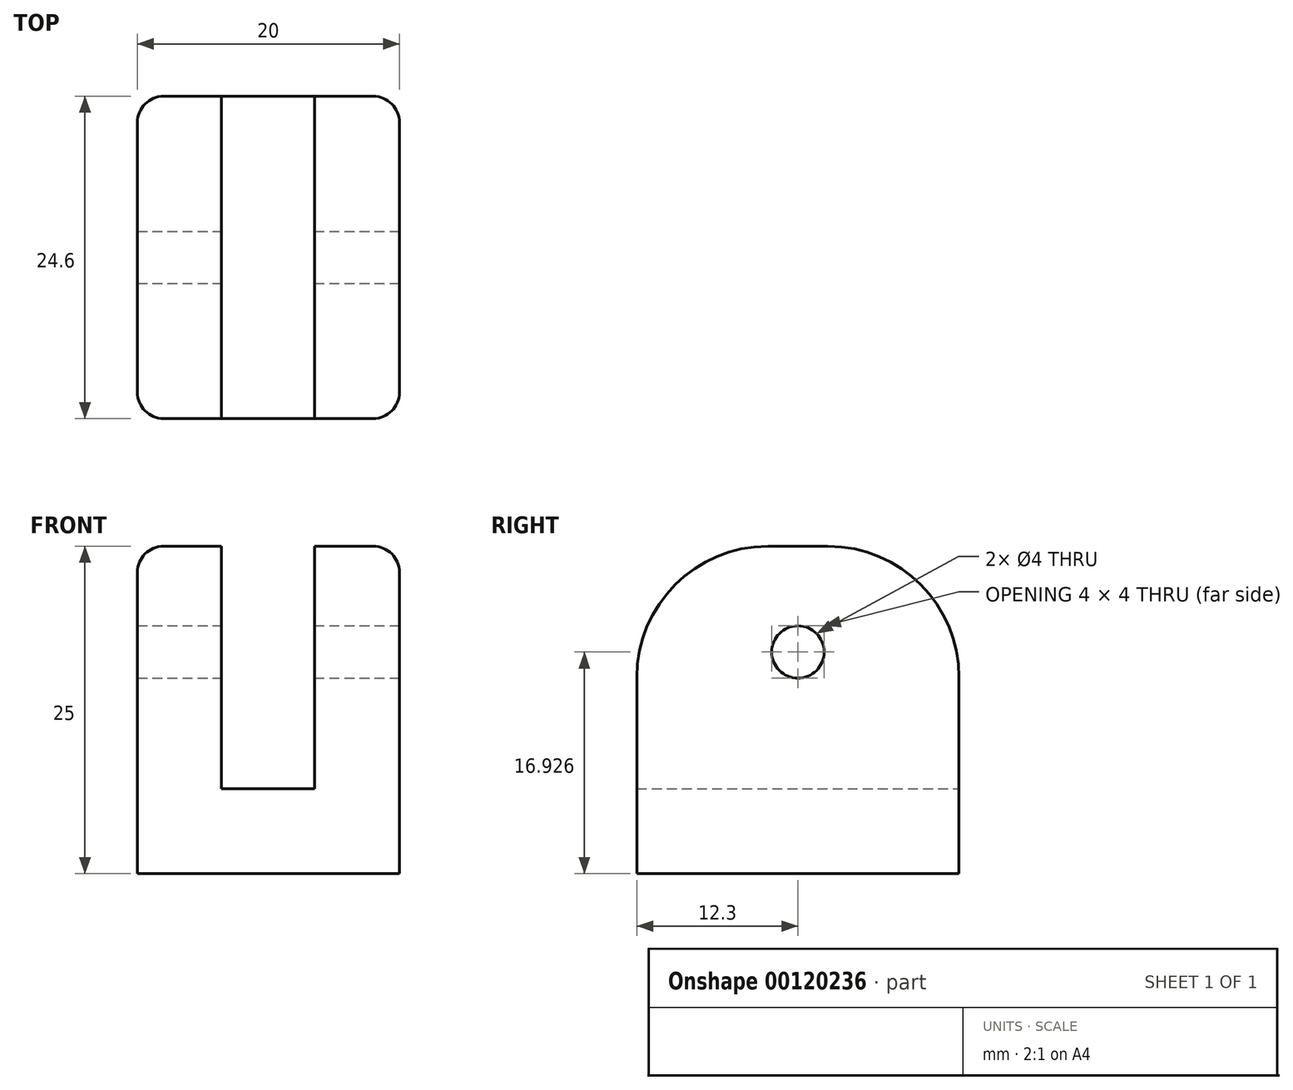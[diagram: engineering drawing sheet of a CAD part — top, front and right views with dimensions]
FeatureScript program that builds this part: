
annotation { "Feature Type Name" : "Feature", "Feature Type Description" : "" }
export const myFeature = defineFeature(function(context is Context, id is Id, definition is map)
    precondition{}
    {
        {
            var Q0;
            Q0=qCreatedBy(makeId("Top.planeOp"),FACE);
            var sketch = newSketch(context, id + "F0", { "sketchPlane" : qUnion([Q0])});
            skLineSegment(sketch, "E0.bottom", {"start": v(10, 12.3) * mm, "end": v(-10, 12.3) * mm});
            skLineSegment(sketch, "E0.top", {"start": v(10, -12.3) * mm, "end": v(-10, -12.3) * mm});
            skLineSegment(sketch, "E0.left", {"start": v(10, 12.3) * mm, "end": v(10, -12.3) * mm});
            skLineSegment(sketch, "E0.right", {"start": v(-10, 12.3) * mm, "end": v(-10, -12.3) * mm});
            skPoint(sketch, "E0.middle", {"position": v(0, 0) * mm});
            skSolve(sketch);
        }
        {
            var Q0;
            Q0=makeQuery(id+"F0.imprint","IMPRINT",FACE,{"disambiguationData":[TD([[makeQuery(id+"F0.imprint","IMPRINT",EDGE,{"derivedFrom":sQuery(id+"F0.wireOp",EDGE,"E0.bottom")}),1.0]])]});
            extrude(context, id + "F1", {"entities" : qUnion([Q0]), "depth" : 25 * mm});
        }
        {
            var Q0;
            Q0=qCreatedBy(makeId("Front.planeOp"),FACE);
            var sketch = newSketch(context, id + "F2", { "sketchPlane" : qUnion([Q0])});
            skLineSegment(sketch, "E1.bottom", {"start": v(-3.59, 6.5) * mm, "end": v(3.51, 6.5) * mm});
            skLineSegment(sketch, "E1.top", {"start": v(-3.6, 26.43) * mm, "end": v(3.5, 26.43) * mm});
            skLineSegment(sketch, "E1.left", {"start": v(-3.6, 6.5) * mm, "end": v(-3.6, 26.43) * mm});
            skLineSegment(sketch, "E1.right", {"start": v(3.51, 6.5) * mm, "end": v(3.5, 26.43) * mm});
            skSolve(sketch);
        }
        {
            var Q0;
            Q0=makeQuery(id+"F2.imprint","IMPRINT",FACE,{"disambiguationData":[TD([[makeQuery(id+"F2.imprint","IMPRINT",EDGE,{"derivedFrom":sQuery(id+"F2.wireOp",EDGE,"E1.bottom")}),1.0]])]});
            extrude(context, id + "F3", {"entities" : qUnion([Q0]), "operationType" : NewBodyOperationType.REMOVE, "endBound" : BoundingType.SYMMETRIC, "depth" : 25 * mm});
        }
        {
            var Q0;
            Q0=makeQuery(id+"F1.opExtrude","SWEPT_FACE",FACE,{"disambiguationData":[OSD([sQuery(id+"F0.wireOp",EDGE,"E0.left")])]});
            var sketch = newSketch(context, id + "F4", { "sketchPlane" : qUnion([Q0])});
            skCircle(sketch, "E2", {"center": v(0, 16.93) * mm, "radius": 2 * mm});
            skSolve(sketch);
        }
        {
            var Q0;
            Q0=makeQuery(id+"F4.imprint","IMPRINT",FACE,{"disambiguationData":[TD([[makeQuery(id+"F4.imprint","IMPRINT",EDGE,{"derivedFrom":sQuery(id+"F4.wireOp",EDGE,"E2")}),1.0]])]});
            var Q1;
            Q1=sQuery(id+"F4.wireOp",EDGE,"E2");
            extrude(context, id + "F5", {"entities" : qUnion([Q0]), "operationType" : NewBodyOperationType.REMOVE, "surfaceEntities" : qUnion([Q1]), "endBound" : BoundingType.THROUGH_ALL, "oppositeDirection" : true, "depth" : 25 * mm});
        }
        {
            var Q0;
            {var subQ0=sQuery(id+"F0.wireOp",EDGE,"E0.right");var subQ1=sQuery(id+"F0.wireOp",EDGE,"E0.top");Q0=makeQuery(id+"F3.boolean.opBoolean","SPLIT",EDGE,{"disambiguationData":[TD([makeQuery(id+"F1.opExtrude","SWEPT_FACE",FACE,{"disambiguationData":[OSD([subQ0])]})])],"derivedFrom":makeQuery(id+"F1.opExtrude","CAP_EDGE",EDGE,{"disambiguationData":[OSD([subQ1])],"isStart":false})});}
            var Q1;
            {var subQ0=sQuery(id+"F0.wireOp",EDGE,"E0.left");var subQ1=sQuery(id+"F0.wireOp",EDGE,"E0.top");Q1=makeQuery(id+"F3.boolean.opBoolean","SPLIT",EDGE,{"disambiguationData":[TD([makeQuery(id+"F1.opExtrude","SWEPT_FACE",FACE,{"disambiguationData":[OSD([subQ0])]})])],"derivedFrom":makeQuery(id+"F1.opExtrude","CAP_EDGE",EDGE,{"disambiguationData":[OSD([subQ1])],"isStart":false})});}
            var Q2;
            {var subQ0=sQuery(id+"F0.wireOp",EDGE,"E0.bottom");var subQ1=sQuery(id+"F0.wireOp",EDGE,"E0.left");Q2=makeQuery(id+"F3.boolean.opBoolean","SPLIT",EDGE,{"disambiguationData":[TD([makeQuery(id+"F1.opExtrude","SWEPT_FACE",FACE,{"disambiguationData":[OSD([subQ1])]})])],"derivedFrom":makeQuery(id+"F1.opExtrude","CAP_EDGE",EDGE,{"disambiguationData":[OSD([subQ0])],"isStart":false})});}
            var Q3;
            {var subQ0=sQuery(id+"F0.wireOp",EDGE,"E0.bottom");var subQ1=sQuery(id+"F0.wireOp",EDGE,"E0.right");Q3=makeQuery(id+"F3.boolean.opBoolean","SPLIT",EDGE,{"disambiguationData":[TD([makeQuery(id+"F1.opExtrude","SWEPT_FACE",FACE,{"disambiguationData":[OSD([subQ1])]})])],"derivedFrom":makeQuery(id+"F1.opExtrude","CAP_EDGE",EDGE,{"disambiguationData":[OSD([subQ0])],"isStart":false})});}
            fillet(context, id + "F6", {"entities" : qUnion([Q0, Q1, Q2, Q3]), "radius" : 10 * mm, "tangentPropagation" : true, "allowEdgeOverflow" : false});
        }
        {
            var Q0;
            {var subQ0=sQuery(id+"F0.wireOp",EDGE,"E0.left");var subQ1=makeQuery(id+"F1.opExtrude","SWEPT_FACE",FACE,{"disambiguationData":[OSD([subQ0])]});var subQ2=sQuery(id+"F0.wireOp",EDGE,"E0.top");Q0=makeQuery(id+"F6.opFillet","BLEND_EDGE",EDGE,{"blendedFrom":[makeQuery(id+"F3.boolean.opBoolean","SPLIT",EDGE,{"disambiguationData":[TD([subQ1])],"derivedFrom":makeQuery(id+"F1.opExtrude","CAP_EDGE",EDGE,{"disambiguationData":[OSD([subQ2])],"isStart":false})}),subQ1],"blendedInto":[subQ1]});}
            var Q1;
            Q1=makeQuery(id+"F1.opExtrude","CAP_EDGE",EDGE,{"disambiguationData":[OSD([sQuery(id+"F0.wireOp",EDGE,"E0.left")])],"isStart":false});
            fillet(context, id + "F7", {"entities" : qUnion([Q0, Q1]), "radius" : 2 * mm, "tangentPropagation" : true, "allowEdgeOverflow" : false});
        }
        {
            var Q0;
            {var subQ0=sQuery(id+"F0.wireOp",EDGE,"E0.right");var subQ1=makeQuery(id+"F1.opExtrude","SWEPT_FACE",FACE,{"disambiguationData":[OSD([subQ0])]});var subQ2=sQuery(id+"F0.wireOp",EDGE,"E0.bottom");Q0=makeQuery(id+"F6.opFillet","BLEND_EDGE",EDGE,{"blendedFrom":[makeQuery(id+"F3.boolean.opBoolean","SPLIT",EDGE,{"disambiguationData":[TD([subQ1])],"derivedFrom":makeQuery(id+"F1.opExtrude","CAP_EDGE",EDGE,{"disambiguationData":[OSD([subQ2])],"isStart":false})}),subQ1],"blendedInto":[subQ1]});}
            fillet(context, id + "F8", {"entities" : qUnion([Q0]), "radius" : 2 * mm, "tangentPropagation" : true, "allowEdgeOverflow" : false});
        }
    });
